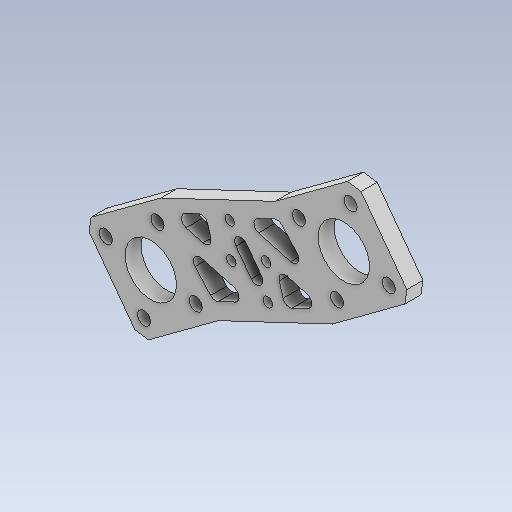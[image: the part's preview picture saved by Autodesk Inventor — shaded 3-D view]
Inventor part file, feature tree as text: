
AUTODESK INVENTOR PART (.ipt)
format: ipt  version: 2020 (Build 240168000, 168)  size: 365,056 bytes
history: native  units: mm
features: sketch x10, extrude x7, reference x6, projected_geometry x6, other x6, hole x3, chamfer x1, fillet x1
ambient origin geometry x8: Origin, YZ Plane, XZ Plane, XY Plane, X Axis, Y Axis, Z Axis, Center Point
bodies: Solid1 (feature_tree)
feature tree (40):
  extrude  "Extrusion1"  Depth=30.0mm
  extrude  "Extrusion2"  Depth=5.0mm TaperAngle=0.0deg
  hole  "Hole1"  [1 undecoded]
  extrude  "Extrusion8"  Depth=20.0mm
  extrude  "Extrusion9"  Depth=10.0mm TaperAngle=0.0deg
  extrude  "Extrusion10"  Depth=30.0mm
  hole  "Hole3"  [1 undecoded]
  chamfer  "Chamfer1"  Distance=3.0mm
  hole  "Hole4"  [1 undecoded]
  extrude  "Extrusion11"  Depth=10.0mm
  fillet  "Fillet1"  Radius=5.0mm
  extrude  "Extrusion12"  Depth=2.0mm TaperAngle=45.0deg
  sketch  "Sketch1"  dims[d0=69.5mm d1=30.0mm]
  reference  "Reference1"
  sketch  "Sketch2"  dims[d2=100.5mm d3=5.0mm d4=0.0mm]
  reference  "Reference2"
  sketch  "Sketch3"  dims[d5=16.0mm d6=5.0mm d7=0.0mm]
  projected_geometry  "Projected Loop1"
  sketch  "Sketch10"  dims[d8=20.0mm d9=20.0mm]
  projected_geometry  "Projected Loop5"
  reference  "Reference8"
  sketch  "Sketch11"  dims[d10=3.0mm d11=6.0mm d12=4.0mm d13=2.0mm d14=90.0deg d15=17.0mm d16=0.0mm d40=10.0mm d41=0.0mm]
  reference  "Reference9"
  reference  "Reference10"
  sketch  "Sketch12"  dims[d42=30.0mm d43=30.0mm]
  projected_geometry  "Projected Loop6"
  sketch  "Sketch13"  dims[d44=5.0mm d45=0.0mm d46=16.0mm]
  projected_geometry  "Projected Loop7"
  sketch  "Sketch14"  dims[d47=20.0mm]
  reference  "Reference11"
  sketch  "Sketch15"  dims[d48=20.0mm]
  projected_geometry  "Projected Loop8"
  sketch  "Sketch16"  dims[d49=3.0mm d50=3.0mm d51=3.0mm d52=3.0mm d53=5.0mm d54=0.0mm d55=4.1mm d56=6.0mm d57=4.0mm d58=2.0mm d59=90.0deg d60=17.0mm d61=0.0mm d62=3.0mm d63=2.0mm d64=45.0deg d65=3.0mm d66=6.0mm d67=4.0mm d68=2.0mm d69=90.0deg d70=17.0mm d71=0.0mm d72=10.0mm d73=0.0mm d74=2.0mm d75=4.0mm d76=4.0mm d77=10.0mm d78=0.0mm]
  projected_geometry  "Projected Loop9"
  parser-record x1  (decoder bookkeeping rows leaked as tree rows — omitted from the tree; the rows remain in map.json)
  other  "reducer_1.iam"
  other  "motor_holder_1:1"
  other  "bearing_8_16_5:1"
  other  "xl_60_out:1"
  other  "slide_holder_2:1"
note: 3 required parameter values undecoded (feature->parameter linkage not recoverable at this tier; creation-order binding heuristic only, values carry confidence <= 0.55)
note: 1 file-system path scrubbed to <path> (originals preserved in map.json)
